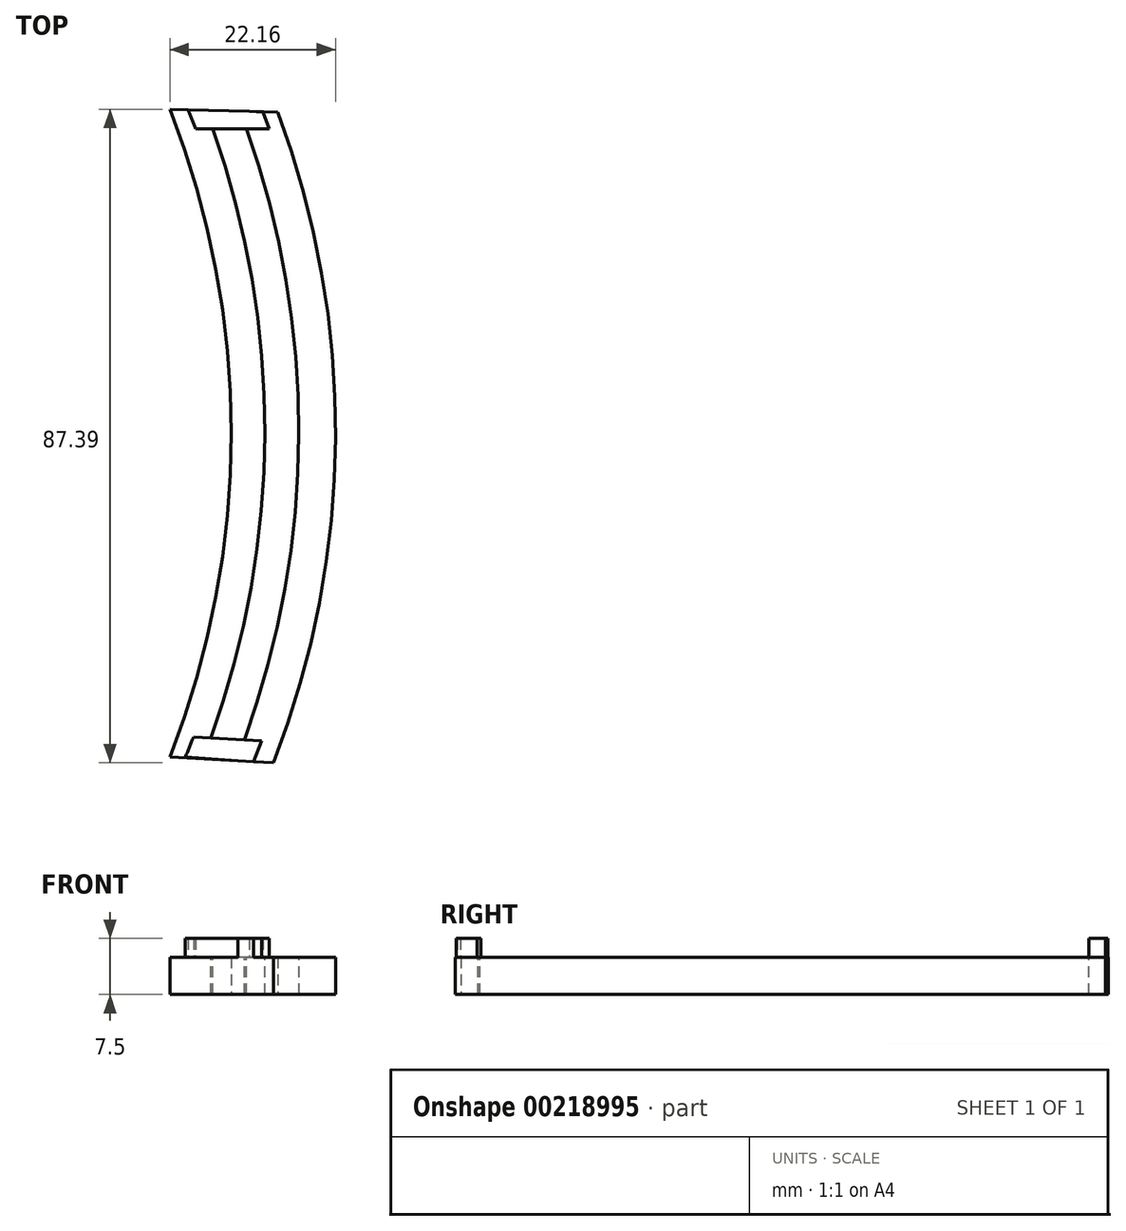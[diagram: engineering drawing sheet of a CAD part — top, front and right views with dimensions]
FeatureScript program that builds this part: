
annotation { "Feature Type Name" : "Feature", "Feature Type Description" : "" }
export const myFeature = defineFeature(function(context is Context, id is Id, definition is map)
    precondition{}
    {
        {
            var Q0;
            Q0=qCreatedBy(makeId("Top.planeOp"),FACE);
            var sketch = newSketch(context, id + "F0", { "sketchPlane" : qUnion([Q0])});
            skArc(sketch, "E0", {"start": v(-9.77, -43.02) * mm, "mid": v(-1.58, 0.3) * mm, "end": v(-9.77, 43.61) * mm});
            skArc(sketch, "E1", {"start": v(4.1, -43.78) * mm, "mid": v(12.39, -0.33) * mm, "end": v(4.67, 43.23) * mm});
            skLineSegment(sketch, "E2", {"start": v(-9.77, 43.61) * mm, "end": v(4.67, 43.23) * mm});
            skLineSegment(sketch, "E3", {"start": v(-9.77, -43.02) * mm, "end": v(4.1, -43.78) * mm});
            skSolve(sketch);
        }
        {
            var Q0;
            Q0 = qSketchRegion(id + "F0", true);
            extrude(context, id + "F1", {"entities" : qUnion([Q0]), "depth" : 5 * mm});
        }
        {
            var Q0;
            Q0=makeQuery(id+"F1.opExtrude","CAP_FACE",FACE,{"disambiguationData":[OSD([sQuery(id+"F0.wireOp",EDGE,"E0"),sQuery(id+"F0.wireOp",EDGE,"E1"),sQuery(id+"F0.wireOp",EDGE,"E2"),sQuery(id+"F0.wireOp",EDGE,"E3")])],"isStart":false});
            var sketch = newSketch(context, id + "F2", { "sketchPlane" : qUnion([Q0])});
            skArc(sketch, "E4", {"start": v(-7.7, -43.03) * mm, "mid": v(1.2, 0.28) * mm, "end": v(-7.4, 43.66) * mm});
            skArc(sketch, "E5", {"start": v(1.4, -43.67) * mm, "mid": v(10.18, -0.33) * mm, "end": v(2.7, 43.26) * mm});
            skLineSegment(sketch, "E6", {"start": v(-6.6, -40.33) * mm, "end": v(2.5, -40.83) * mm});
            skLineSegment(sketch, "E7", {"start": v(3.5, 41.01) * mm, "end": v(-6.35, 41.01) * mm});
            skLineSegment(sketch, "E8", {"start": v(3.5, 41.01) * mm, "end": v(2.7, 43.26) * mm});
            skLineSegment(sketch, "E9", {"start": v(-7.4, 43.66) * mm, "end": v(-6.35, 41.01) * mm});
            skLineSegment(sketch, "E10", {"start": v(1.4, -43.67) * mm, "end": v(2.5, -40.83) * mm});
            skLineSegment(sketch, "E11", {"start": v(-6.6, -40.33) * mm, "end": v(-7.7, -43.03) * mm});
            skLineSegment(sketch, "E12", {"start": v(1.4, -43.67) * mm, "end": v(-7.7, -43.03) * mm});
            skLineSegment(sketch, "E13", {"start": v(2.7, 43.26) * mm, "end": v(-7.4, 43.66) * mm});
            skSolve(sketch);
        }
        {
            var Q0;
            {var subQ4=sQuery(id+"F2.wireOp",EDGE,"E7");Q0=makeQuery(id+"F2.imprint","IMPRINT",FACE,{"disambiguationData":[TD([[makeQuery(id+"F2.imprint","IMPRINT",EDGE,{"derivedFrom":subQ4}),-1.0]])]});}
            var Q1;
            {var subQ7=sQuery(id+"F2.wireOp",EDGE,"E6");Q1=makeQuery(id+"F2.imprint","IMPRINT",FACE,{"disambiguationData":[TD([[makeQuery(id+"F2.imprint","IMPRINT",EDGE,{"derivedFrom":subQ7}),-1.0]])]});}
            extrude(context, id + "F3", {"entities" : qUnion([Q0, Q1]), "operationType" : NewBodyOperationType.ADD, "depth" : 2.5 * mm});
        }
        {
            var Q0;
            Q0=makeQuery(id+"F1.opExtrude","CAP_FACE",FACE,{"disambiguationData":[OSD([sQuery(id+"F0.wireOp",EDGE,"E0"),sQuery(id+"F0.wireOp",EDGE,"E1"),sQuery(id+"F0.wireOp",EDGE,"E2"),sQuery(id+"F0.wireOp",EDGE,"E3")])],"isStart":false});
            var sketch = newSketch(context, id + "F4", { "sketchPlane" : qUnion([Q0])});
            skLineSegment(sketch, "E14", {"start": v(-4.3, -40.45) * mm, "end": v(0.2, -40.7) * mm});
            skLineSegment(sketch, "E15", {"start": v(-4.05, 41.01) * mm, "end": v(0.45, 41.01) * mm});
            skArc(sketch, "E16", {"start": v(-4.3, -40.45) * mm, "mid": v(2.95, 0.26) * mm, "end": v(-4.05, 41.01) * mm});
            skArc(sketch, "E17", {"start": v(0.2, -40.7) * mm, "mid": v(7.5, 0.13) * mm, "end": v(0.45, 41.01) * mm});
            skSolve(sketch);
        }
        {
            var Q0;
            Q0=makeQuery(id+"F4.imprint","IMPRINT",FACE,{"disambiguationData":[TD([[makeQuery(id+"F4.imprint","IMPRINT",EDGE,{"derivedFrom":sQuery(id+"F4.wireOp",EDGE,"E14")}),1.0]])]});
            extrude(context, id + "F5", {"entities" : qUnion([Q0]), "operationType" : NewBodyOperationType.REMOVE, "oppositeDirection" : true, "depth" : 25 * mm});
        }
    });
